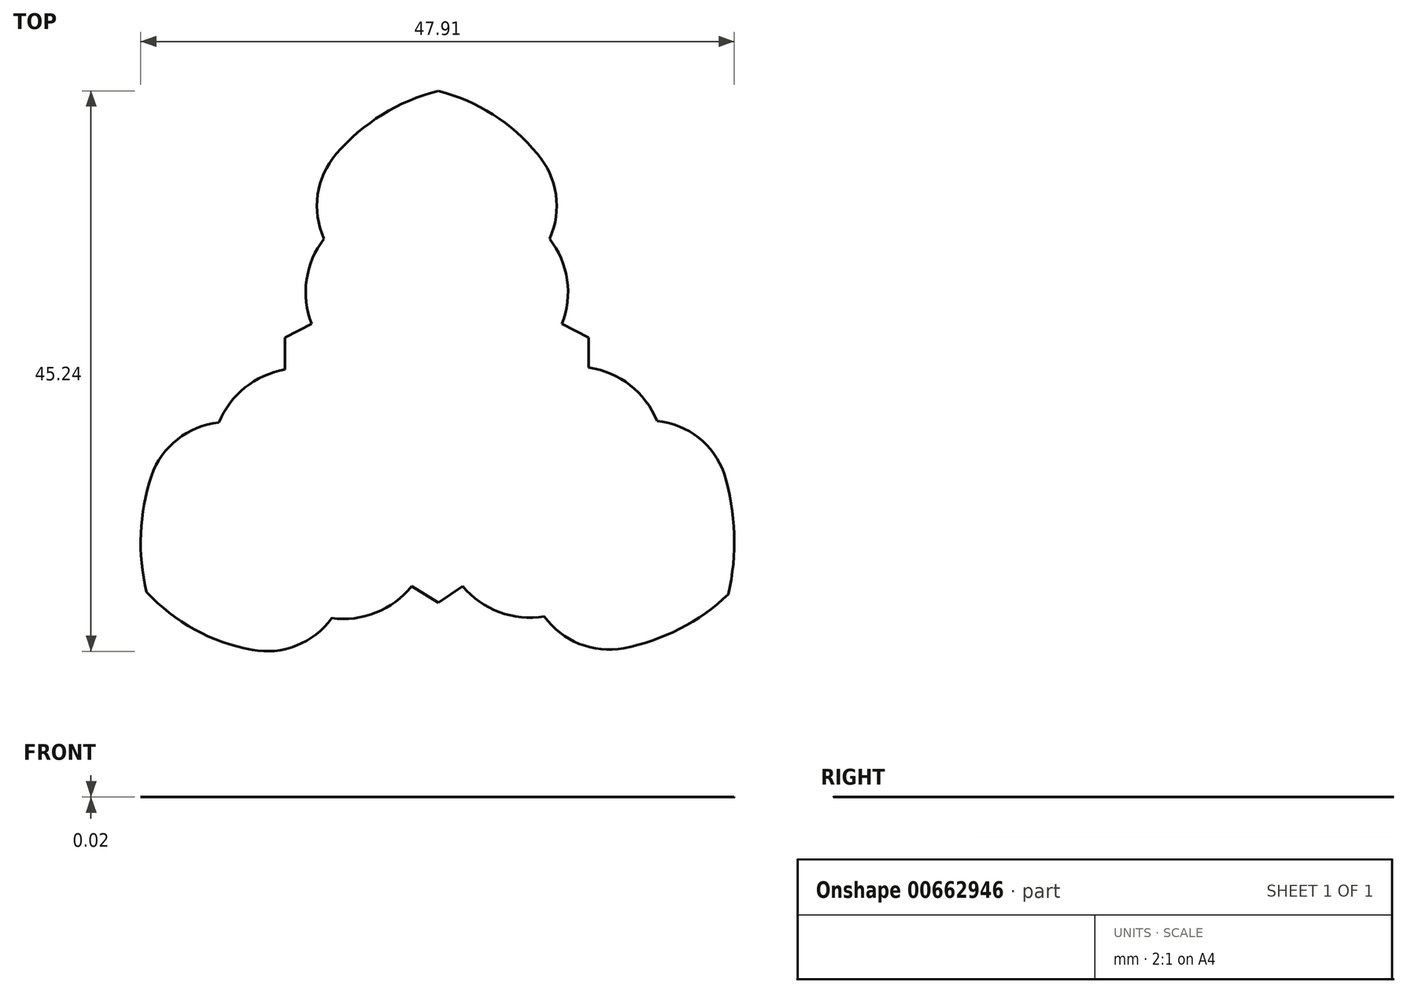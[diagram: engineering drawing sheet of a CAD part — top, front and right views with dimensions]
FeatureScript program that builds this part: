
annotation { "Feature Type Name" : "Feature", "Feature Type Description" : "" }
export const myFeature = defineFeature(function(context is Context, id is Id, definition is map)
    precondition{}
    {
        {
            var Q0;
            Q0=qCreatedBy(makeId("Top.planeOp"),FACE);
            var sketch = newSketch(context, id + "F0", { "sketchPlane" : qUnion([Q0])});
            skPoint(sketch, "E0.center", {"position": v(0, 0) * mm});
            skArc(sketch, "E1", {"start": v(-8.23, 21.98) * mm, "mid": v(-9.72, 18.7) * mm, "end": v(-9.2, 15.13) * mm});
            skArc(sketch, "E2", {"start": v(-9.2, 15.13) * mm, "mid": v(-10.62, 11.82) * mm, "end": v(-10.2, 8.25) * mm});
            skLineSegment(sketch, "E3", {"start": v(-10.2, 8.25) * mm, "end": v(-12.37, 7.15) * mm});
            skLineSegment(sketch, "E4", {"start": v(-12.37, 7.15) * mm, "end": v(-12.37, 4.64) * mm});
            skLineSegment(sketch, "E5.MirrorCS", {"start": v(12.16, 7.15) * mm, "end": v(12.16, 4.64) * mm});
            skLineSegment(sketch, "E6.MirrorCS", {"start": v(10, 8.25) * mm, "end": v(12.16, 7.15) * mm});
            skArc(sketch, "E7.MirrorCS", {"start": v(9, 15.13) * mm, "mid": v(10.4, 11.82) * mm, "end": v(10, 8.25) * mm});
            skArc(sketch, "E8.MirrorCS", {"start": v(8.01, 21.98) * mm, "mid": v(9.5, 18.7) * mm, "end": v(9, 15.13) * mm});
            skArc(sketch, "E9", {"start": v(23.1, -3.85) * mm, "mid": v(21, -0.92) * mm, "end": v(17.66, 0.43) * mm});
            skArc(sketch, "E10", {"start": v(17.66, 0.43) * mm, "mid": v(15.48, 3.32) * mm, "end": v(12.16, 4.74) * mm});
            skArc(sketch, "E11.MirrorCS", {"start": v(8.56, -15.34) * mm, "mid": v(4.94, -15) * mm, "end": v(1.97, -12.9) * mm});
            skArc(sketch, "E12.MirrorCS", {"start": v(14.98, -17.91) * mm, "mid": v(11.4, -17.56) * mm, "end": v(8.56, -15.34) * mm});
            skLineSegment(sketch, "E13", {"start": v(1.97, -12.9) * mm, "end": v(0, -14.26) * mm});
            skLineSegment(sketch, "E14", {"start": v(0, -14.26) * mm, "end": v(-2.14, -12.9) * mm});
            skArc(sketch, "E15", {"start": v(-15.02, -18.05) * mm, "mid": v(-11.43, -17.7) * mm, "end": v(-8.6, -15.48) * mm});
            skArc(sketch, "E16", {"start": v(-8.6, -15.48) * mm, "mid": v(-5.03, -15.05) * mm, "end": v(-2.14, -12.9) * mm});
            skArc(sketch, "E17.MirrorCS", {"start": v(-17.7, 0.28) * mm, "mid": v(-15.6, 3.12) * mm, "end": v(-12.37, 4.57) * mm});
            skArc(sketch, "E18.MirrorCS", {"start": v(-23.14, -4) * mm, "mid": v(-21.05, -1.06) * mm, "end": v(-17.7, 0.28) * mm});
            skLineSegment(sketch, "E19", {"start": v(-12.37, 4.64) * mm, "end": v(-12.37, 4.57) * mm});
            skArc(sketch, "E20", {"start": v(0, 27.07) * mm, "mid": v(-4.5, 25.16) * mm, "end": v(-8.23, 21.98) * mm});
            skArc(sketch, "E21", {"start": v(8.01, 21.98) * mm, "mid": v(4.42, 25.17) * mm, "end": v(0, 27.07) * mm});
            skArc(sketch, "E22", {"start": v(23.42, -13.56) * mm, "mid": v(23.89, -8.68) * mm, "end": v(23.1, -3.85) * mm});
            skArc(sketch, "E23", {"start": v(14.98, -17.91) * mm, "mid": v(19.52, -16.35) * mm, "end": v(23.42, -13.56) * mm});
            skArc(sketch, "E24", {"start": v(-23.14, -4) * mm, "mid": v(-24, -8.66) * mm, "end": v(-23.53, -13.39) * mm});
            skArc(sketch, "E25", {"start": v(-23.53, -13.39) * mm, "mid": v(-19.66, -16.41) * mm, "end": v(-15.02, -18.05) * mm});
            skSolve(sketch);
        }
        {
            var Q0;
            Q0=makeQuery(id+"F0.imprint","IMPRINT",FACE,{"disambiguationData":[TD([[makeQuery(id+"F0.imprint","IMPRINT",EDGE,{"derivedFrom":sQuery(id+"F0.wireOp",EDGE,"E1")}),1.0]])]});
            extrude(context, id + "F1", {"entities" : qUnion([Q0]), "depth" : 7 / 406.4 * mm, "offsetDistance" : 25.4 * mm});
        }
    });
